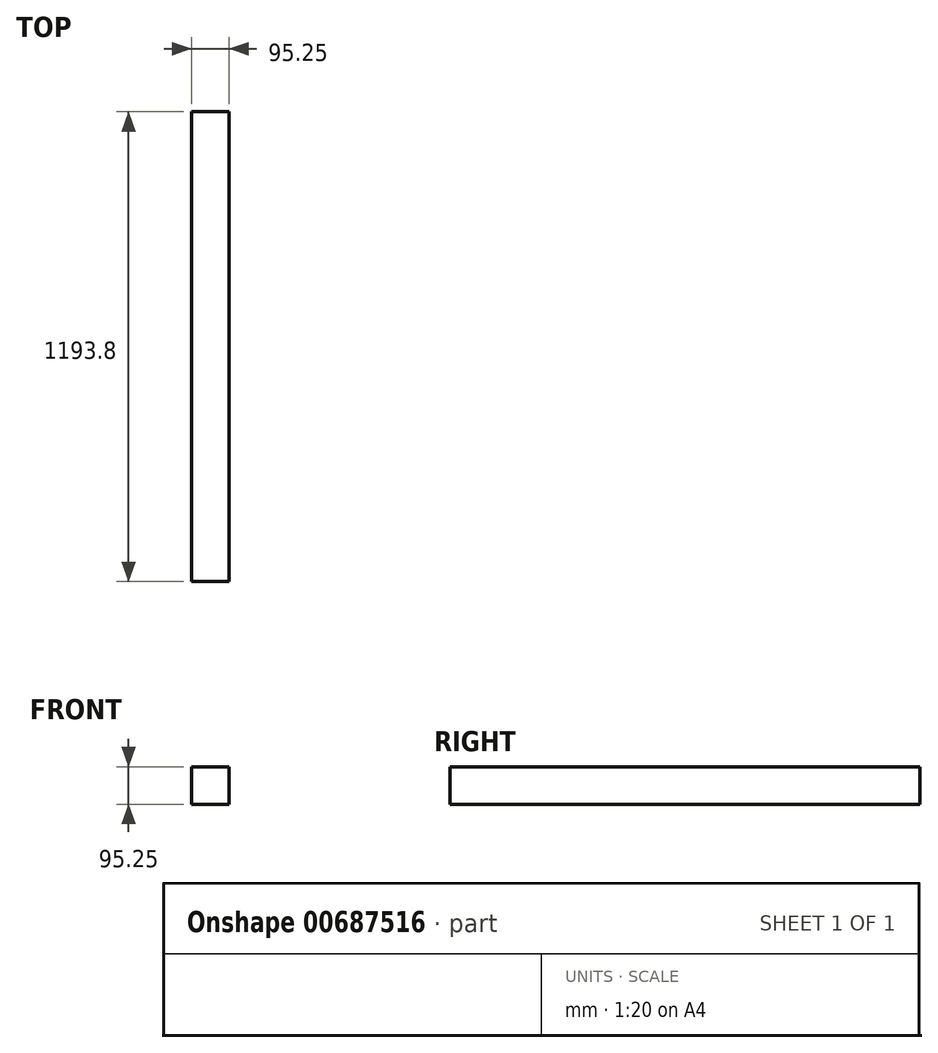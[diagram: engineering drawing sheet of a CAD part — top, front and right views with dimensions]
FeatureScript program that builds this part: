
annotation { "Feature Type Name" : "Feature", "Feature Type Description" : "" }
export const myFeature = defineFeature(function(context is Context, id is Id, definition is map)
    precondition{}
    {
        {
            var Q0;
            Q0=qCreatedBy(makeId("Front.planeOp"),FACE);
            var sketch = newSketch(context, id + "F0", { "sketchPlane" : qUnion([Q0])});
            skLineSegment(sketch, "E0.bottom", {"start": v(0, 0) * mm, "end": v(95.25, 0) * mm});
            skLineSegment(sketch, "E0.top", {"start": v(0, 95.25) * mm, "end": v(95.25, 95.25) * mm});
            skLineSegment(sketch, "E0.left", {"start": v(0, 0) * mm, "end": v(0, 95.25) * mm});
            skLineSegment(sketch, "E0.right", {"start": v(95.25, 0) * mm, "end": v(95.25, 95.25) * mm});
            skSolve(sketch);
        }
        {
            var Q0;
            Q0=makeQuery(id+"F0.imprint","IMPRINT",FACE,{"disambiguationData":[TD([[makeQuery(id+"F0.imprint","IMPRINT",EDGE,{"derivedFrom":sQuery(id+"F0.wireOp",EDGE,"E0.bottom")}),1.0]])]});
            extrude(context, id + "F1", {"entities" : qUnion([Q0]), "depth" : 1193.8 * mm, "offsetDistance" : 25.4 * mm});
        }
    });
